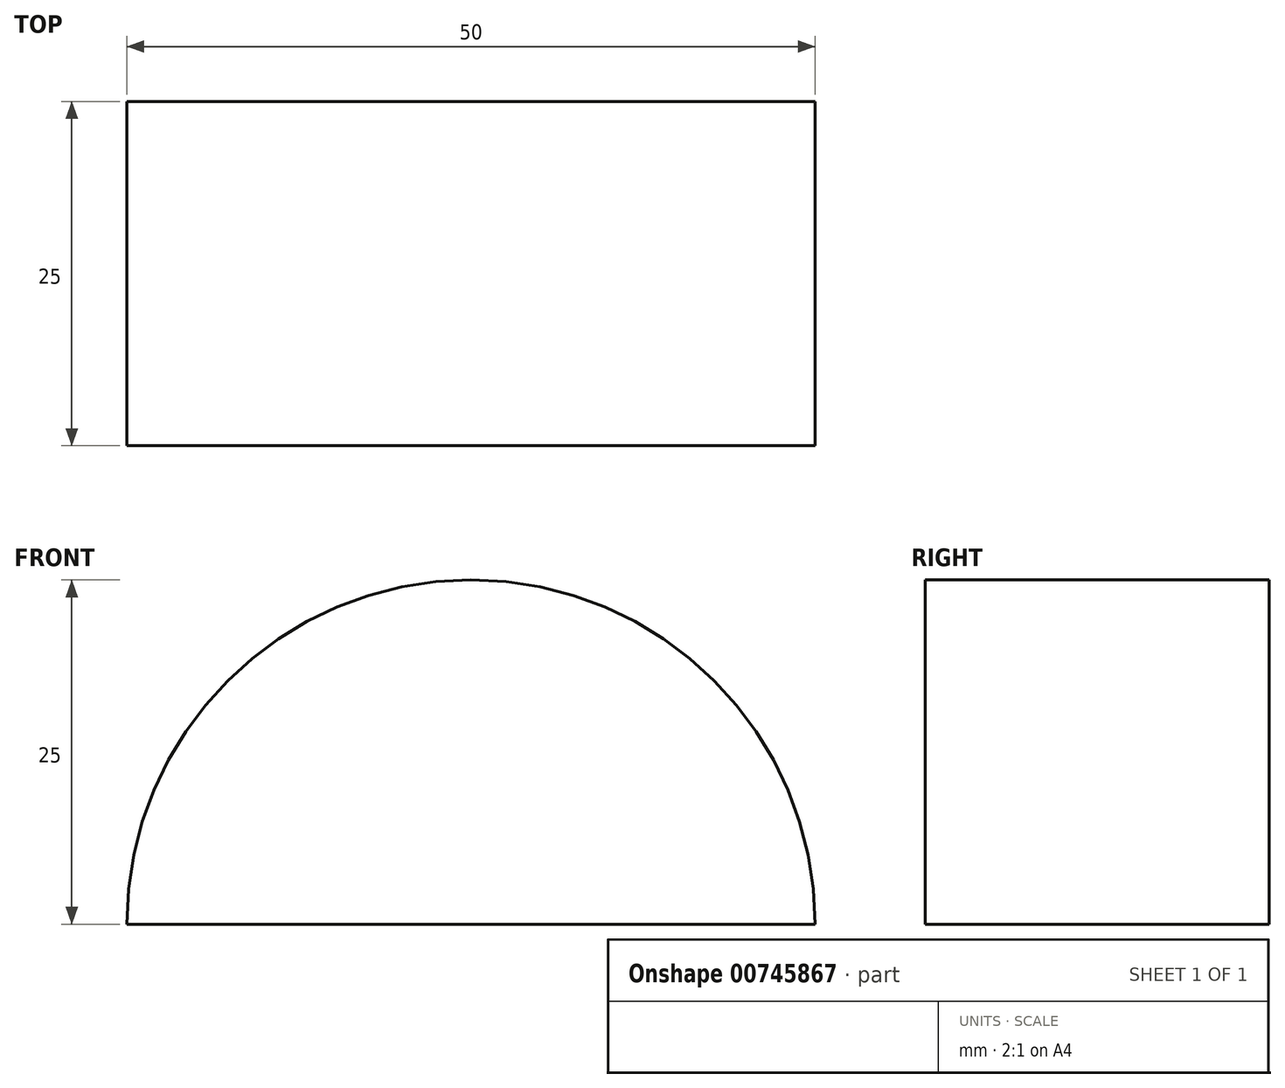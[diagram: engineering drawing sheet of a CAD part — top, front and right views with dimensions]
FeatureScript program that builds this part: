
annotation { "Feature Type Name" : "Feature", "Feature Type Description" : "" }
export const myFeature = defineFeature(function(context is Context, id is Id, definition is map)
    precondition{}
    {
        {
            var Q0;
            Q0=qCreatedBy(makeId("Front.planeOp"),FACE);
            var sketch = newSketch(context, id + "F0", { "sketchPlane" : qUnion([Q0])});
            skArc(sketch, "E0", {"start": v(25, 0) * mm, "mid": v(0, 25) * mm, "end": v(-25, 0) * mm});
            skLineSegment(sketch, "E1", {"start": v(0, 25) * mm, "end": v(0, -175) * mm});
            skLineSegment(sketch, "E2", {"start": v(-25, 0) * mm, "end": v(25, 0) * mm});
            skLineSegment(sketch, "E3", {"start": v(-10, 0) * mm, "end": v(-10, -64.4) * mm});
            skLineSegment(sketch, "E4.MirrorCS", {"start": v(10, 0) * mm, "end": v(10, -64.4) * mm});
            skSolve(sketch);
        }
        {
            var Q0;
            Q0 = qSketchRegion(id + "F0", true);
            extrude(context, id + "F1", {"entities" : qUnion([Q0]), "depth" : 25 * mm, "offsetDistance" : 25 * mm});
        }
    });
